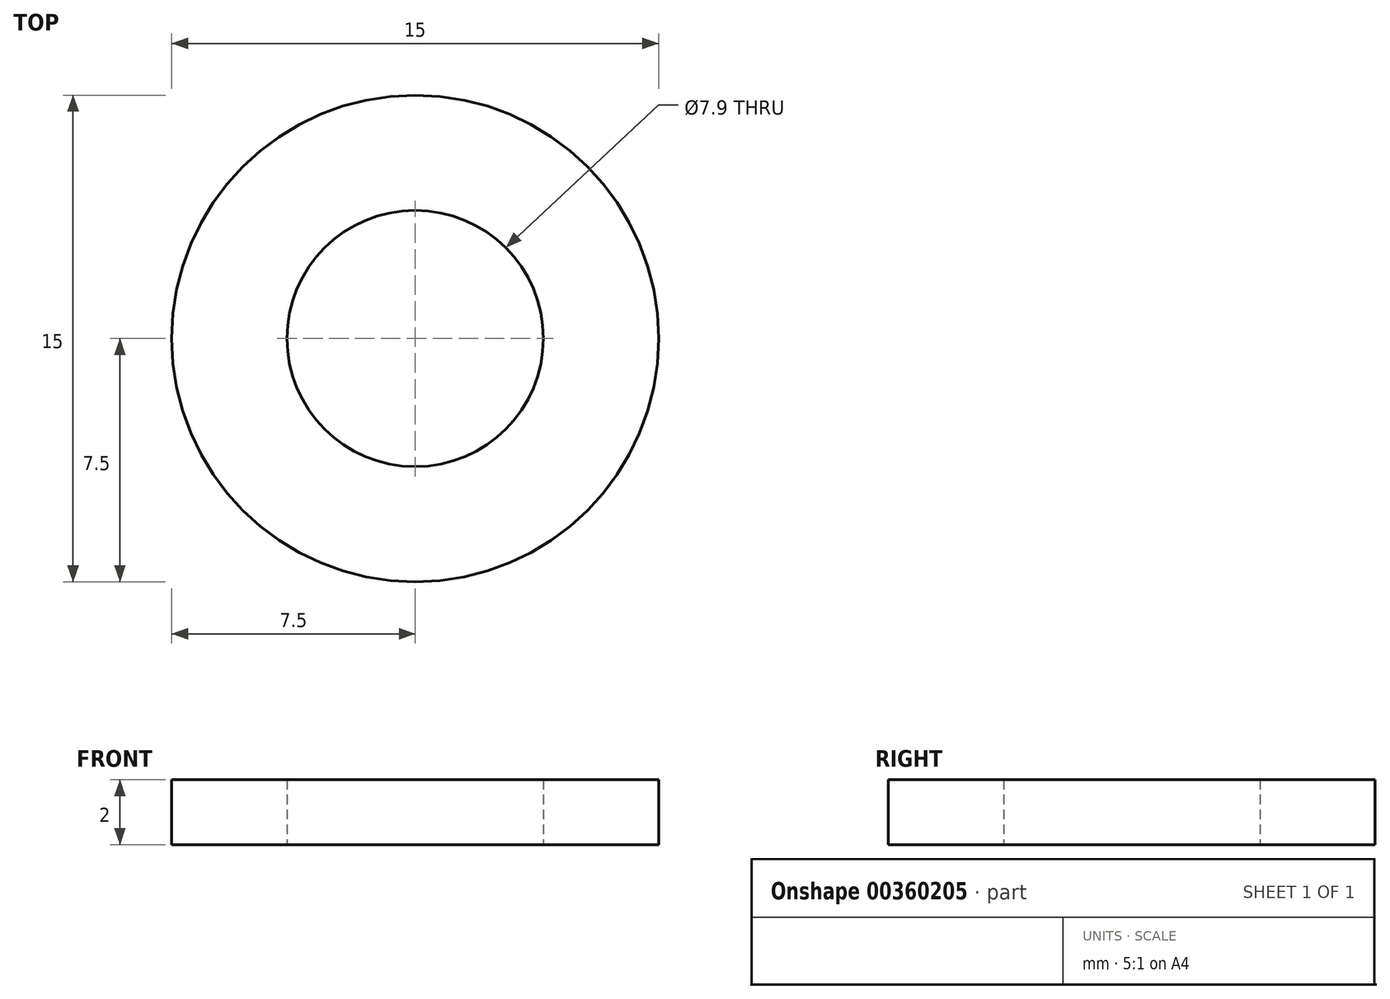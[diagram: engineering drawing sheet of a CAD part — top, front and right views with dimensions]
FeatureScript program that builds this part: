
annotation { "Feature Type Name" : "Feature", "Feature Type Description" : "" }
export const myFeature = defineFeature(function(context is Context, id is Id, definition is map)
    precondition{}
    {
        {
            var Q0;
            Q0=qCreatedBy(makeId("Top.planeOp"),FACE);
            var sketch = newSketch(context, id + "F0", { "sketchPlane" : qUnion([Q0])});
            skCircle(sketch, "E0", {"center": v(0, 0) * mm, "radius": 2.7 * mm});
            skCircle(sketch, "E1", {"center": v(0, 0) * mm, "radius": 3.95 * mm});
            skCircle(sketch, "E2", {"center": v(0, 0) * mm, "radius": 7.5 * mm});
            skSolve(sketch);
        }
        {
            var Q0;
            Q0=makeQuery(id+"F0.imprint","IMPRINT",FACE,{"disambiguationData":[TD([[makeQuery(id+"F0.imprint","IMPRINT",EDGE,{"derivedFrom":sQuery(id+"F0.wireOp",EDGE,"E1")}),-1.0]])]});
            extrude(context, id + "F1", {"entities" : qUnion([Q0]), "offsetDistance" : 25 * mm, "depth" : 2 * mm});
        }
    });
